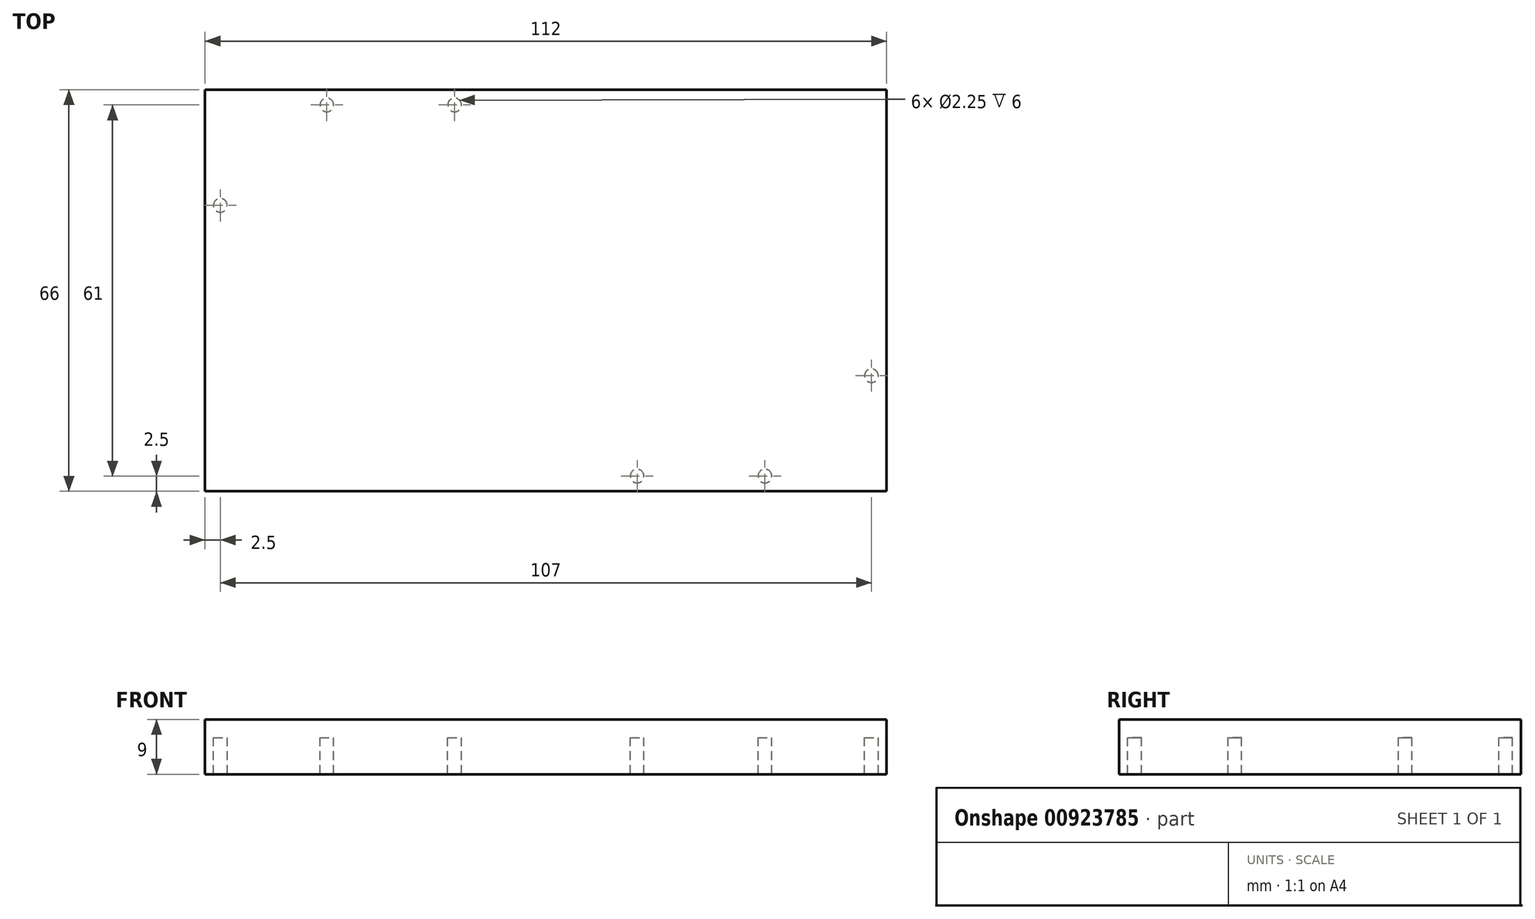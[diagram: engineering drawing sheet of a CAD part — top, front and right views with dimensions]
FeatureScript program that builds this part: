
annotation { "Feature Type Name" : "Feature", "Feature Type Description" : "" }
export const myFeature = defineFeature(function(context is Context, id is Id, definition is map)
    precondition{}
    {
        {
            var Q0;
            Q0=qCreatedBy(makeId("Top.planeOp"),FACE);
            var sketch = newSketch(context, id + "F0", { "sketchPlane" : qUnion([Q0])});
            skLineSegment(sketch, "E0.bottom", {"start": v(-56, 33) * mm, "end": v(56, 33) * mm});
            skLineSegment(sketch, "E0.top", {"start": v(-56, -33) * mm, "end": v(56, -33) * mm});
            skLineSegment(sketch, "E0.left", {"start": v(-56, 33) * mm, "end": v(-56, -33) * mm});
            skLineSegment(sketch, "E0.right", {"start": v(56, 33) * mm, "end": v(56, -33) * mm});
            skPoint(sketch, "E0.middle", {"position": v(0, 0) * mm});
            skSolve(sketch);
        }
        {
            var Q0;
            Q0 = qSketchRegion(id + "F0", true);
            extrude(context, id + "F1", {"entities" : qUnion([Q0]), "depth" : 3 * mm, "offsetDistance" : 25 * mm});
        }
        {
            var Q0;
            Q0=makeQuery(id+"F1.opExtrude","CAP_FACE",FACE,{"disambiguationData":[OSD([sQuery(id+"F0.wireOp",EDGE,"E0.bottom"),sQuery(id+"F0.wireOp",EDGE,"E0.top"),sQuery(id+"F0.wireOp",EDGE,"E0.left"),sQuery(id+"F0.wireOp",EDGE,"E0.right")])],"isStart":true});
            var sketch = newSketch(context, id + "F2", { "sketchPlane" : qUnion([Q0])});
            skCircle(sketch, "E1", {"center": v(-36, 30.5) * mm, "radius": 1.13 * mm});
            skCircle(sketch, "E2", {"center": v(-15, 30.5) * mm, "radius": 1.13 * mm});
            skCircle(sketch, "E3.MirrorC", {"center": v(15, 30.5) * mm, "radius": 1.13 * mm});
            skCircle(sketch, "E4.MirrorC", {"center": v(36, 30.5) * mm, "radius": 1.13 * mm});
            skCircle(sketch, "E5.MirrorC", {"center": v(-36, -30.5) * mm, "radius": 1.13 * mm});
            skCircle(sketch, "E6.MirrorC", {"center": v(-15, -30.5) * mm, "radius": 1.13 * mm});
            skCircle(sketch, "E7.MirrorC", {"center": v(15, -30.5) * mm, "radius": 1.13 * mm});
            skCircle(sketch, "E8.MirrorC", {"center": v(36, -30.5) * mm, "radius": 1.13 * mm});
            skCircle(sketch, "E9", {"center": v(-53.5, 14) * mm, "radius": 1.13 * mm});
            skCircle(sketch, "E10.MirrorC", {"center": v(-53.5, -14) * mm, "radius": 1.13 * mm});
            skCircle(sketch, "E11.MirrorC", {"center": v(53.5, 14) * mm, "radius": 1.13 * mm});
            skCircle(sketch, "E12.MirrorC", {"center": v(53.5, -14) * mm, "radius": 1.13 * mm});
            skSolve(sketch);
        }
        {
            var Q0;
            Q0=makeQuery(id+"F2.imprint","IMPRINT",FACE,{"disambiguationData":[TD([[makeQuery(id+"F2.imprint","IMPRINT",EDGE,{"derivedFrom":sQuery(id+"F2.wireOp",EDGE,"E9")}),1.0]])]});
            var Q1;
            Q1=makeQuery(id+"F2.imprint","IMPRINT",FACE,{"disambiguationData":[TD([[makeQuery(id+"F2.imprint","IMPRINT",EDGE,{"derivedFrom":sQuery(id+"F2.wireOp",EDGE,"E1")}),1.0]])]});
            var Q2;
            Q2=makeQuery(id+"F2.imprint","IMPRINT",FACE,{"disambiguationData":[TD([[makeQuery(id+"F2.imprint","IMPRINT",EDGE,{"derivedFrom":sQuery(id+"F2.wireOp",EDGE,"E2")}),1.0]])]});
            var Q3;
            Q3=makeQuery(id+"F2.imprint","IMPRINT",FACE,{"disambiguationData":[TD([[makeQuery(id+"F2.imprint","IMPRINT",EDGE,{"derivedFrom":sQuery(id+"F2.wireOp",EDGE,"E3.MirrorC")}),-1.0]])]});
            var Q4;
            Q4=makeQuery(id+"F2.imprint","IMPRINT",FACE,{"disambiguationData":[TD([[makeQuery(id+"F2.imprint","IMPRINT",EDGE,{"derivedFrom":sQuery(id+"F2.wireOp",EDGE,"E4.MirrorC")}),-1.0]])]});
            var Q5;
            Q5=makeQuery(id+"F2.imprint","IMPRINT",FACE,{"disambiguationData":[TD([[makeQuery(id+"F2.imprint","IMPRINT",EDGE,{"derivedFrom":sQuery(id+"F2.wireOp",EDGE,"E11.MirrorC")}),-1.0]])]});
            var Q6;
            Q6=makeQuery(id+"F2.imprint","IMPRINT",FACE,{"disambiguationData":[TD([[makeQuery(id+"F2.imprint","IMPRINT",EDGE,{"derivedFrom":sQuery(id+"F2.wireOp",EDGE,"E12.MirrorC")}),1.0]])]});
            var Q7;
            Q7=makeQuery(id+"F2.imprint","IMPRINT",FACE,{"disambiguationData":[TD([[makeQuery(id+"F2.imprint","IMPRINT",EDGE,{"derivedFrom":sQuery(id+"F2.wireOp",EDGE,"E8.MirrorC")}),1.0]])]});
            var Q8;
            Q8=makeQuery(id+"F2.imprint","IMPRINT",FACE,{"disambiguationData":[TD([[makeQuery(id+"F2.imprint","IMPRINT",EDGE,{"derivedFrom":sQuery(id+"F2.wireOp",EDGE,"E7.MirrorC")}),1.0]])]});
            var Q9;
            Q9=makeQuery(id+"F2.imprint","IMPRINT",FACE,{"disambiguationData":[TD([[makeQuery(id+"F2.imprint","IMPRINT",EDGE,{"derivedFrom":sQuery(id+"F2.wireOp",EDGE,"E6.MirrorC")}),-1.0]])]});
            var Q10;
            Q10=makeQuery(id+"F2.imprint","IMPRINT",FACE,{"disambiguationData":[TD([[makeQuery(id+"F2.imprint","IMPRINT",EDGE,{"derivedFrom":sQuery(id+"F2.wireOp",EDGE,"E5.MirrorC")}),-1.0]])]});
            var Q11;
            Q11=makeQuery(id+"F2.imprint","IMPRINT",FACE,{"disambiguationData":[TD([[makeQuery(id+"F2.imprint","IMPRINT",EDGE,{"derivedFrom":sQuery(id+"F2.wireOp",EDGE,"E10.MirrorC")}),-1.0]])]});
            extrude(context, id + "F3", {"entities" : qUnion([Q0, Q1, Q2, Q3, Q4, Q5, Q6, Q7, Q8, Q9, Q10, Q11]), "operationType" : NewBodyOperationType.ADD, "depth" : 6 * mm, "offsetDistance" : 25 * mm});
        }
    });
